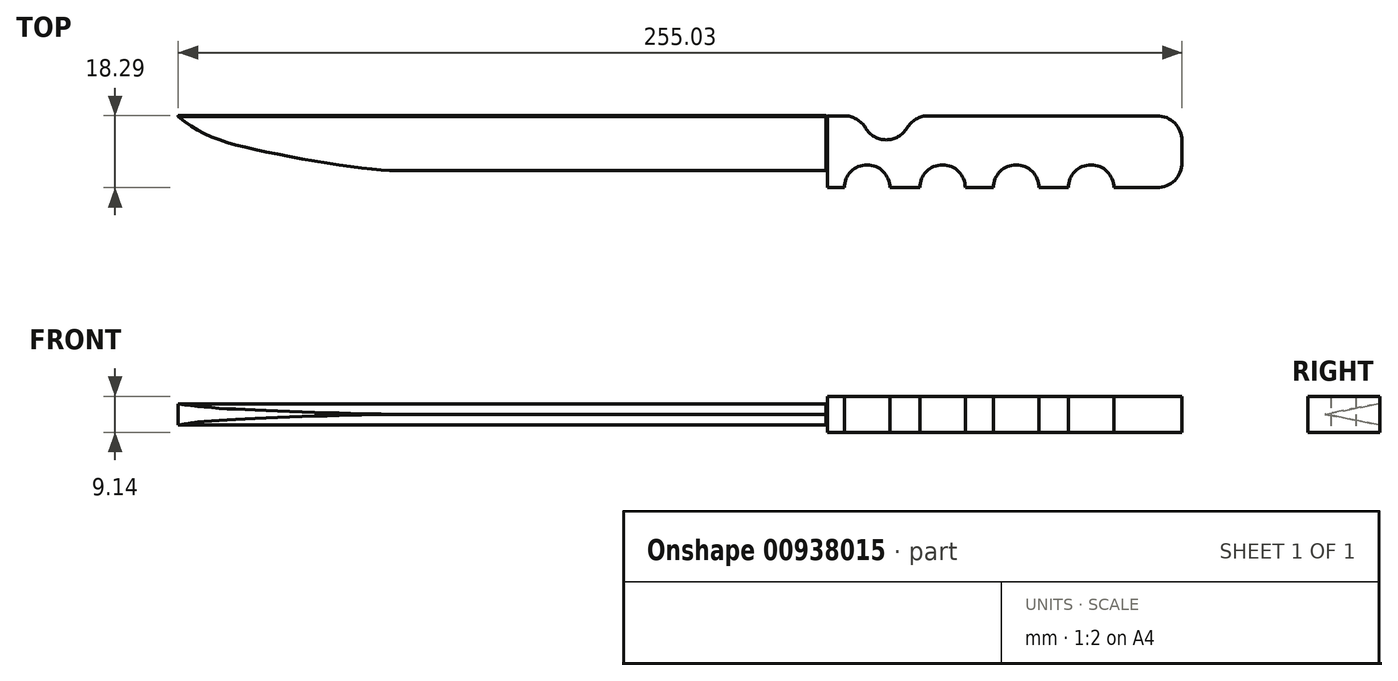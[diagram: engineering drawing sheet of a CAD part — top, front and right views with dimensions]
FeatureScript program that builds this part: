
annotation { "Feature Type Name" : "Feature", "Feature Type Description" : "" }
export const myFeature = defineFeature(function(context is Context, id is Id, definition is map)
    precondition{}
    {
        {
            var Q0;
            Q0=qCreatedBy(makeId("Top.planeOp"),FACE);
            var sketch = newSketch(context, id + "F0", { "sketchPlane" : qUnion([Q0])});
            skLineSegment(sketch, "E0", {"start": v(60.62, 6.16) * mm, "end": v(60.62, 24.41) * mm});
            skLineSegment(sketch, "E1.bottom", {"start": v(60.62, 24.41) * mm, "end": v(64.82, 24.41) * mm});
            skLineSegment(sketch, "E1.top", {"start": v(60.62, 6.16) * mm, "end": v(64.87, 6.16) * mm});
            skLineSegment(sketch, "E1.right", {"start": v(150.67, 18.06) * mm, "end": v(150.67, 12.51) * mm});
            skArc(sketch, "E2", {"start": v(76.44, 6.16) * mm, "mid": v(70.66, 11.95) * mm, "end": v(64.87, 6.16) * mm});
            skArc(sketch, "E3", {"start": v(95.6, 6.16) * mm, "mid": v(89.82, 11.95) * mm, "end": v(84.03, 6.16) * mm});
            skArc(sketch, "E4", {"start": v(114.32, 6.16) * mm, "mid": v(108.53, 11.95) * mm, "end": v(102.74, 6.16) * mm});
            skArc(sketch, "E5", {"start": v(133.33, 6.16) * mm, "mid": v(127.54, 11.95) * mm, "end": v(121.76, 6.16) * mm});
            skArc(sketch, "E6", {"start": v(70.28, 21.3) * mm, "mid": v(75.52, 18.32) * mm, "end": v(80.76, 21.3) * mm});
            skLineSegment(sketch, "E7.trimOffspring", {"start": v(86.22, 24.41) * mm, "end": v(144.32, 24.41) * mm});
            skLineSegment(sketch, "E8.trimOffspring", {"start": v(133.33, 6.16) * mm, "end": v(144.32, 6.16) * mm});
            skLineSegment(sketch, "E9.trimOffspring", {"start": v(114.32, 6.16) * mm, "end": v(121.76, 6.16) * mm});
            skLineSegment(sketch, "E10.trimOffspring", {"start": v(95.6, 6.16) * mm, "end": v(102.74, 6.16) * mm});
            skLineSegment(sketch, "E11.trimOffspring", {"start": v(76.44, 6.16) * mm, "end": v(84.03, 6.16) * mm});
            skPoint(sketch, "E12.visualSharp", {"position": v(81.61, 24.41) * mm});
            skArc(sketch, "E12.filletArc", {"start": v(86.22, 24.41) * mm, "mid": v(83.08, 23.58) * mm, "end": v(80.76, 21.3) * mm});
            skPoint(sketch, "E13.visualSharp", {"position": v(69.43, 24.41) * mm});
            skArc(sketch, "E13.filletArc", {"start": v(70.28, 21.3) * mm, "mid": v(67.97, 23.58) * mm, "end": v(64.82, 24.41) * mm});
            skPoint(sketch, "E14.visualSharp", {"position": v(150.67, 24.41) * mm});
            skArc(sketch, "E14.filletArc", {"start": v(150.67, 18.06) * mm, "mid": v(148.8, 22.55) * mm, "end": v(144.32, 24.41) * mm});
            skPoint(sketch, "E15.visualSharp", {"position": v(150.67, 6.16) * mm});
            skArc(sketch, "E15.filletArc", {"start": v(144.32, 6.16) * mm, "mid": v(148.8, 8.02) * mm, "end": v(150.67, 12.51) * mm});
            skSolve(sketch);
        }
        {
            var Q0;
            Q0=qCreatedBy(makeId("Top.planeOp"),FACE);
            var sketch = newSketch(context, id + "F1", { "sketchPlane" : qUnion([Q0])});
            skLineSegment(sketch, "E16", {"start": v(60.23, 24.45) * mm, "end": v(-104.36, 24.45) * mm});
            skFitSpline(sketch, "E17", {"points": [v(-104.36, 24.45) * mm, v(-84.86, 15.97) * mm, v(-48.99, 10.45) * mm], "startDerivative": vector(36.6, -31.63) * mm, "endDerivative": vector(35.1, 0) * mm});
            skLineSegment(sketch, "E18", {"start": v(-48.99, 10.45) * mm, "end": v(60.23, 10.45) * mm});
            skLineSegment(sketch, "E19", {"start": v(60.23, 10.45) * mm, "end": v(60.23, 24.45) * mm});
            skSolve(sketch);
        }
        {
            var Q0;
            Q0=makeQuery(id+"F1.imprint","IMPRINT",FACE,{"disambiguationData":[TD([[makeQuery(id+"F1.imprint","IMPRINT",EDGE,{"derivedFrom":sQuery(id+"F1.wireOp",EDGE,"E16")}),1.0]])]});
            var Q1;
            Q1=sQuery(id+"F1.wireOp",EDGE,"E18");
            revolve(context, id + "F2", {"surfaceOperationType" : NewSurfaceOperationType.NEW, "entities" : qUnion([Q0]), "axis" : qUnion([Q1]), "revolveType" : RevolveType.SYMMETRIC, "oppositeDirection" : true, "angle" : 22 * degree});
        }
        {
            var Q0;
            Q0=makeQuery(id+"F0.imprint","IMPRINT",FACE,{"disambiguationData":[TD([[makeQuery(id+"F0.imprint","IMPRINT",EDGE,{"derivedFrom":sQuery(id+"F0.wireOp",EDGE,"E0")}),-1.0]])]});
            extrude(context, id + "F3", {"entities" : qUnion([Q0]), "endBound" : BoundingType.SYMMETRIC, "depth" : 9.14 * mm, "offsetDistance" : 25.4 * mm});
        }
    });
